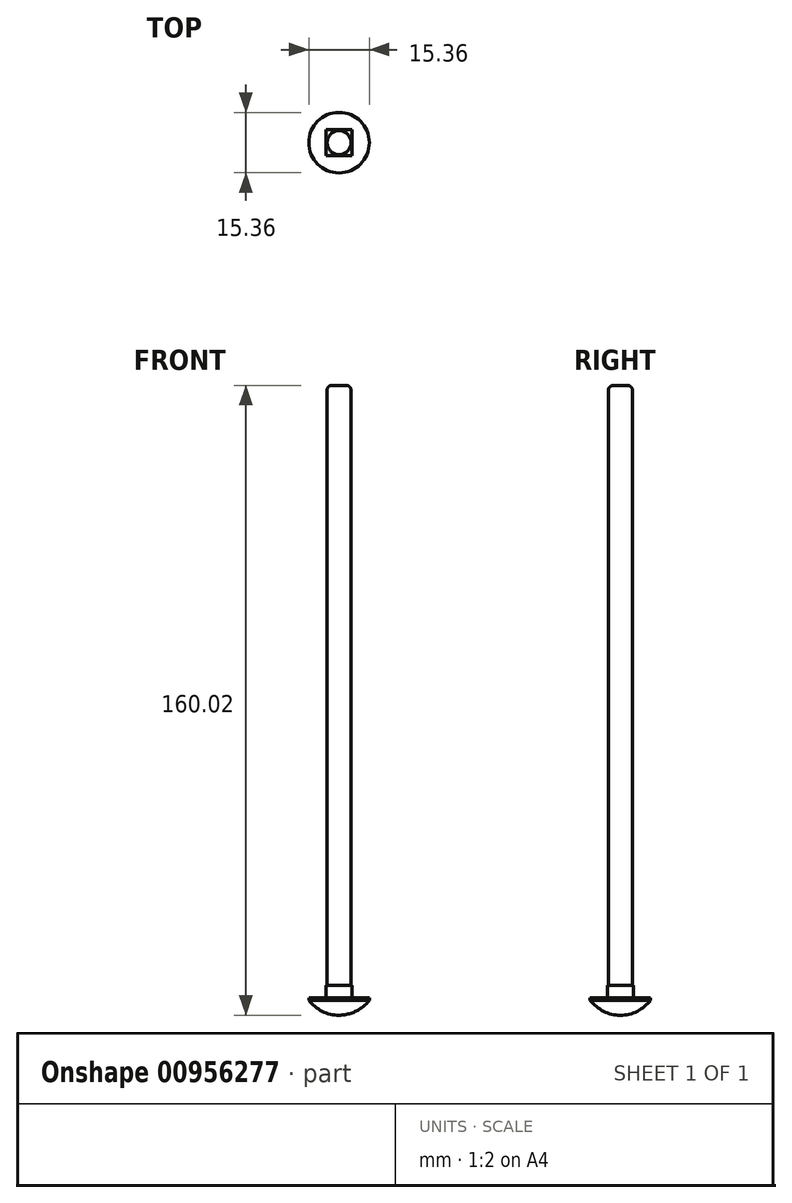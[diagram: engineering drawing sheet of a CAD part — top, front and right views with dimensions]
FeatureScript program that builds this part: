
annotation { "Feature Type Name" : "Feature", "Feature Type Description" : "" }
export const myFeature = defineFeature(function(context is Context, id is Id, definition is map)
    precondition{}
    {
        {
            var Q0;
            Q0=qCreatedBy(makeId("Top.planeOp"),FACE);
            var sketch = newSketch(context, id + "F0", { "sketchPlane" : qUnion([Q0])});
            skCircle(sketch, "E0", {"center": v(0, 0) * mm, "radius": 3.05 * mm});
            skSolve(sketch);
        }
        {
            var Q0;
            Q0 = qSketchRegion(id + "F0", true);
            extrude(context, id + "F1", {"entities" : qUnion([Q0]), "depth" : 152.4 * mm, "offsetDistance" : 25.4 * mm});
        }
        {
            var Q0;
            Q0=qCreatedBy(makeId("Top.planeOp"),FACE);
            var sketch = newSketch(context, id + "F2", { "sketchPlane" : qUnion([Q0])});
            skLineSegment(sketch, "E1.bottom", {"start": v(-3.26, -3.26) * mm, "end": v(3.26, -3.26) * mm});
            skLineSegment(sketch, "E1.top", {"start": v(-3.26, 3.26) * mm, "end": v(3.26, 3.26) * mm});
            skLineSegment(sketch, "E1.left", {"start": v(-3.26, -3.26) * mm, "end": v(-3.26, 3.26) * mm});
            skLineSegment(sketch, "E1.right", {"start": v(3.26, -3.26) * mm, "end": v(3.26, 3.26) * mm});
            skPoint(sketch, "E1.middle", {"position": v(0, 0) * mm});
            skSolve(sketch);
        }
        {
            var Q0;
            Q0 = qSketchRegion(id + "F2", true);
            extrude(context, id + "F3", {"entities" : qUnion([Q0]), "operationType" : NewBodyOperationType.ADD, "oppositeDirection" : true, "depth" : 3.17 * mm, "offsetDistance" : 25.4 * mm});
        }
        {
            var Q0;
            Q0=makeQuery(id+"F3.opExtrude","CAP_FACE",FACE,{"disambiguationData":[OSD([sQuery(id+"F2.wireOp",EDGE,"E1.bottom"),sQuery(id+"F2.wireOp",EDGE,"E1.top"),sQuery(id+"F2.wireOp",EDGE,"E1.left"),sQuery(id+"F2.wireOp",EDGE,"E1.right")])],"isStart":false});
            var sketch = newSketch(context, id + "F4", { "sketchPlane" : qUnion([Q0])});
            skCircle(sketch, "E2", {"center": v(0, 0) * mm, "radius": 7.68 * mm});
            skSolve(sketch);
        }
        {
            var Q0;
            Q0 = qSketchRegion(id + "F4", true);
            extrude(context, id + "F5", {"entities" : qUnion([Q0]), "operationType" : NewBodyOperationType.ADD, "depth" : 0.64 * mm, "offsetDistance" : 25.4 * mm});
        }
        {
            var Q0;
            Q0=qCreatedBy(makeId("Front.planeOp"),FACE);
            var sketch = newSketch(context, id + "F6", { "sketchPlane" : qUnion([Q0])});
            skArc(sketch, "E3", {"start": v(0, -7.62) * mm, "mid": v(4.29, -6.62) * mm, "end": v(7.68, -3.8) * mm});
            skLineSegment(sketch, "E4", {"start": v(0, -3.81) * mm, "end": v(0, -7.62) * mm});
            skPoint(sketch, "E5.orphan", {"position": v(-7.68, -3.8) * mm});
            skLineSegment(sketch, "E6", {"start": v(0, -3.81) * mm, "end": v(7.68, -3.8) * mm});
            skSolve(sketch);
        }
        {
            var Q0;
            Q0=makeQuery(id+"F6.imprint","IMPRINT",FACE,{"disambiguationData":[TD([[makeQuery(id+"F6.imprint","IMPRINT",EDGE,{"derivedFrom":sQuery(id+"F6.wireOp",EDGE,"E3")}),1.0]])]});
            var Q1;
            Q1=sQuery(id+"F6.wireOp",EDGE,"E4");
            revolve(context, id + "F7", {"operationType" : NewBodyOperationType.ADD, "surfaceOperationType" : NewSurfaceOperationType.NEW, "entities" : qUnion([Q0]), "axis" : qUnion([Q1]), "revolveType" : RevolveType.FULL});
        }
        {
            var Q0;
            Q0=makeQuery(id+"F1.opExtrude","CAP_EDGE",EDGE,{"disambiguationData":[OSD([sQuery(id+"F0.wireOp",EDGE,"E0")])],"isStart":false});
            fillet(context, id + "F8", {"entities" : qUnion([Q0]), "radius" : 1.27 * mm, "tangentPropagation" : true, "allowEdgeOverflow" : false});
        }
    });
